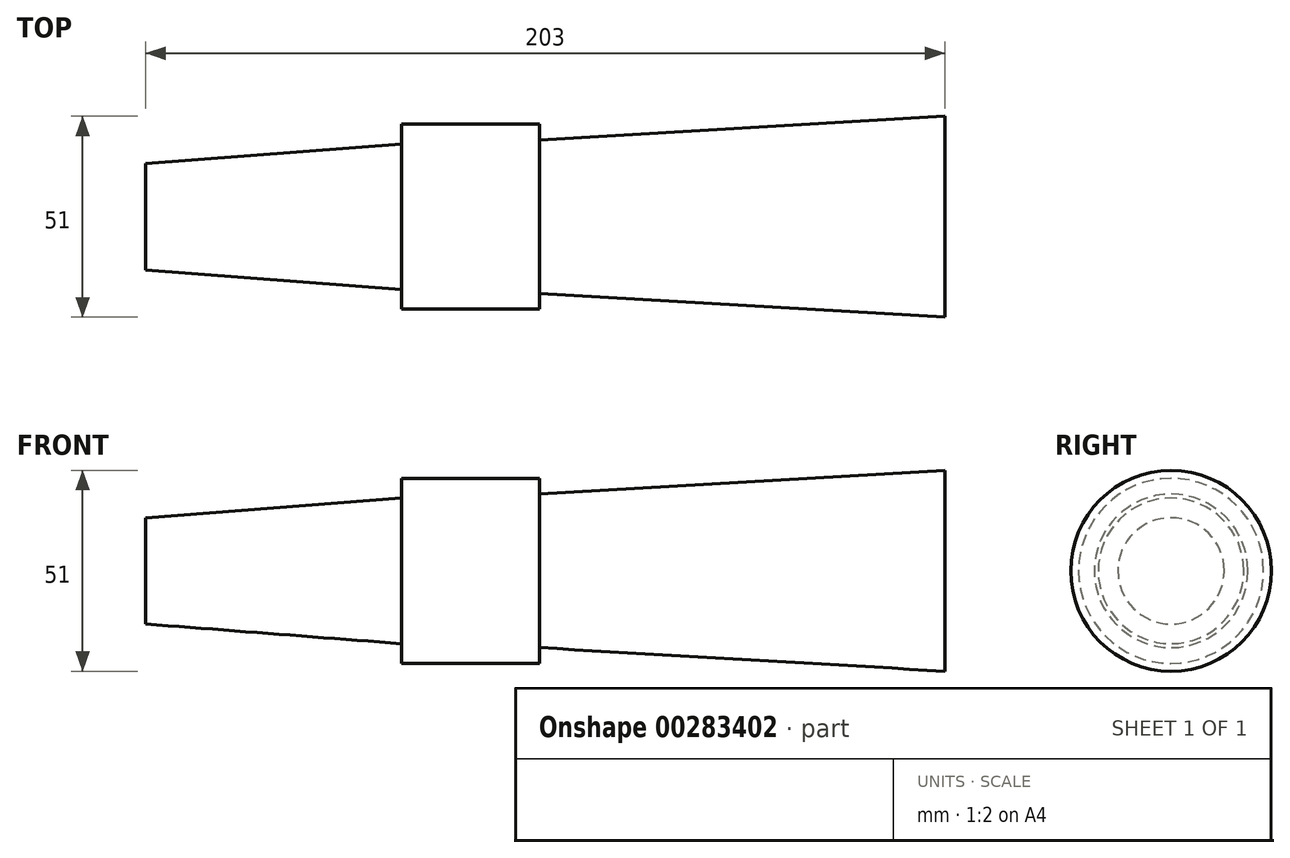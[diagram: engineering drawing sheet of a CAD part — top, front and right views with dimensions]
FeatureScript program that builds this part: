
annotation { "Feature Type Name" : "Feature", "Feature Type Description" : "" }
export const myFeature = defineFeature(function(context is Context, id is Id, definition is map)
    precondition{}
    {
        {
            var Q0;
            Q0=qCreatedBy(makeId("Front.planeOp"),FACE);
            var sketch = newSketch(context, id + "F0", { "sketchPlane" : qUnion([Q0])});
            skLineSegment(sketch, "E0", {"start": v(0, 0) * mm, "end": v(0, 13.5) * mm});
            skLineSegment(sketch, "E1", {"start": v(0, 13.5) * mm, "end": v(65, 18.5) * mm});
            skLineSegment(sketch, "E2", {"start": v(65, 18.5) * mm, "end": v(65, 23.5) * mm});
            skLineSegment(sketch, "E3", {"start": v(65, 23.5) * mm, "end": v(100, 23.5) * mm});
            skLineSegment(sketch, "E4", {"start": v(100, 23.5) * mm, "end": v(100, 19.5) * mm});
            skLineSegment(sketch, "E5", {"start": v(100, 19.5) * mm, "end": v(203, 25.5) * mm});
            skLineSegment(sketch, "E6", {"start": v(203, 25.5) * mm, "end": v(203, 0) * mm});
            skLineSegment(sketch, "E7", {"start": v(380.52, 0) * mm, "end": v(-40.07, 0) * mm, "construction": true});
            skLineSegment(sketch, "E8", {"start": v(0, 0) * mm, "end": v(203, 0) * mm});
            skLineSegment(sketch, "E9.MirrorCS", {"start": v(100, -23.5) * mm, "end": v(100, -19.5) * mm});
            skLineSegment(sketch, "E10.MirrorCS", {"start": v(65, -18.5) * mm, "end": v(65, -23.5) * mm});
            skLineSegment(sketch, "E11.MirrorCS", {"start": v(100, -19.5) * mm, "end": v(203, -25.5) * mm});
            skLineSegment(sketch, "E12.MirrorCS", {"start": v(65, -23.5) * mm, "end": v(100, -23.5) * mm});
            skLineSegment(sketch, "E13.MirrorCS", {"start": v(0, -13.5) * mm, "end": v(65, -18.5) * mm});
            skLineSegment(sketch, "E14.MirrorCS", {"start": v(203, -25.5) * mm, "end": v(203, 0) * mm});
            skLineSegment(sketch, "E15.MirrorCS", {"start": v(0, 0) * mm, "end": v(0, -13.5) * mm});
            skLineSegment(sketch, "E16", {"start": v(65, 18.5) * mm, "end": v(65, 0) * mm, "construction": true});
            skLineSegment(sketch, "E17", {"start": v(100, 19.5) * mm, "end": v(100, 0) * mm, "construction": true});
            skLineSegment(sketch, "E18", {"start": v(0, 50) * mm, "end": v(203, 50) * mm});
            skLineSegment(sketch, "E19", {"start": v(203, 50) * mm, "end": v(203, 90) * mm});
            skLineSegment(sketch, "E20", {"start": v(203, 90) * mm, "end": v(0, 90) * mm});
            skLineSegment(sketch, "E21", {"start": v(0, 90) * mm, "end": v(0, 50) * mm});
            skLineSegment(sketch, "E22", {"start": v(0, 70) * mm, "end": v(203, 70) * mm, "construction": true});
            skLineSegment(sketch, "E23", {"start": v(65, 23.5) * mm, "end": v(65, 70) * mm, "construction": true});
            skLineSegment(sketch, "E24", {"start": v(100, 23.5) * mm, "end": v(100, 70) * mm, "construction": true});
            skLineSegment(sketch, "E25", {"start": v(203, 25.5) * mm, "end": v(203, 70) * mm, "construction": true});
            skLineSegment(sketch, "E26", {"start": v(0, 13.5) * mm, "end": v(0, 70) * mm, "construction": true});
            skLineSegment(sketch, "E27", {"start": v(203, 25.5) * mm, "end": v(229, 25.5) * mm});
            skLineSegment(sketch, "E28", {"start": v(229, 25.5) * mm, "end": v(229, 40) * mm});
            skLineSegment(sketch, "E29", {"start": v(229, 40) * mm, "end": v(259, 40) * mm});
            skLineSegment(sketch, "E30", {"start": v(259, 40) * mm, "end": v(259, 0) * mm});
            skLineSegment(sketch, "E31", {"start": v(203, 0) * mm, "end": v(259, 0) * mm});
            skLineSegment(sketch, "E32.MirrorCS", {"start": v(259, -40) * mm, "end": v(259, 0) * mm});
            skLineSegment(sketch, "E33.MirrorCS", {"start": v(229, -40) * mm, "end": v(259, -40) * mm});
            skLineSegment(sketch, "E34.MirrorCS", {"start": v(229, -25.5) * mm, "end": v(229, -40) * mm});
            skLineSegment(sketch, "E35.MirrorCS", {"start": v(203, -25.5) * mm, "end": v(229, -25.5) * mm});
            skLineSegment(sketch, "E36", {"start": v(259, 14.77) * mm, "end": v(309.03, 14.77) * mm});
            skLineSegment(sketch, "E37", {"start": v(309.03, 14.77) * mm, "end": v(309.03, -14.77) * mm});
            skLineSegment(sketch, "E38", {"start": v(309.03, -14.77) * mm, "end": v(259, -14.77) * mm});
            skSolve(sketch);
        }
        {
            var Q0;
            Q0=makeQuery(id+"F0.imprint","IMPRINT",FACE,{"disambiguationData":[TD([[makeQuery(id+"F0.imprint","IMPRINT",EDGE,{"derivedFrom":sQuery(id+"F0.wireOp",EDGE,"E0")}),-1.0]])]});
            var Q1;
            Q1=sQuery(id+"F0.wireOp",EDGE,"E7");
            revolve(context, id + "F1", {"entities" : qUnion([Q0]), "axis" : qUnion([Q1]), "revolveType" : RevolveType.FULL});
        }
    });
